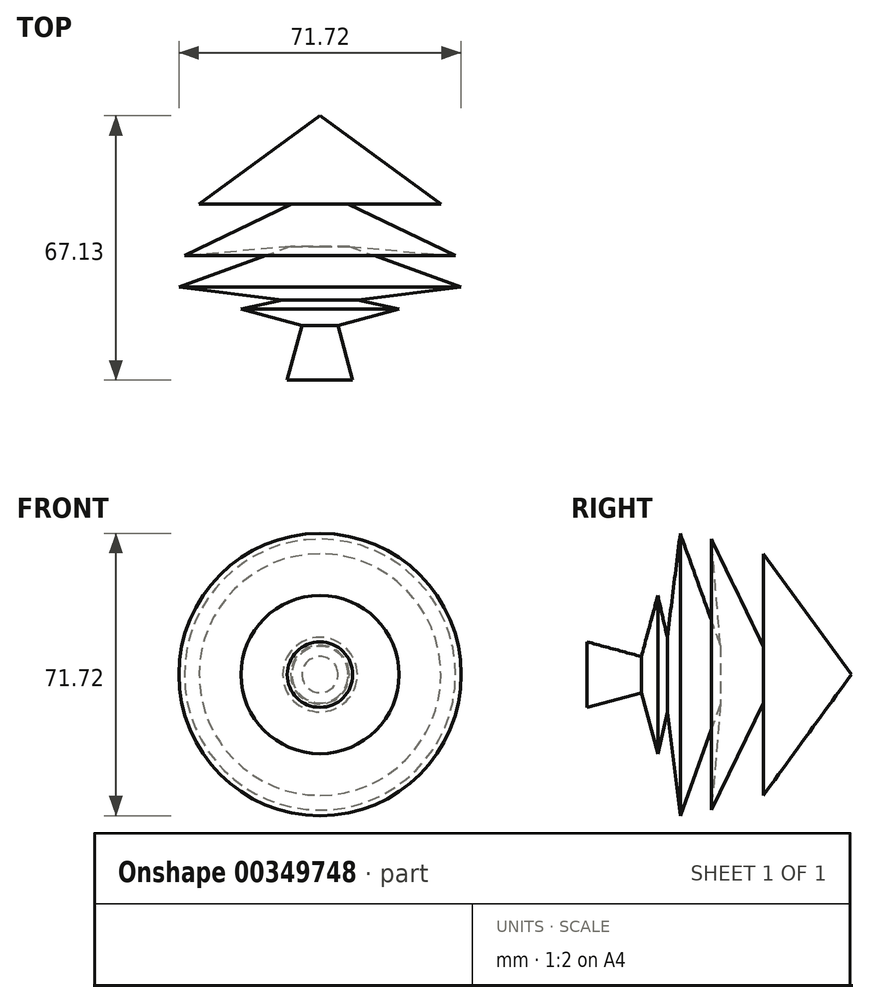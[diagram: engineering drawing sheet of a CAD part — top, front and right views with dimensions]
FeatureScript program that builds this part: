
annotation { "Feature Type Name" : "Feature", "Feature Type Description" : "" }
export const myFeature = defineFeature(function(context is Context, id is Id, definition is map)
    precondition{}
    {
        {
            var Q0;
            Q0=qCreatedBy(makeId("Top.planeOp"),FACE);
            var sketch = newSketch(context, id + "F0", { "sketchPlane" : qUnion([Q0])});
            skLineSegment(sketch, "E0", {"start": v(-8.32, -23.67) * mm, "end": v(-4.6, -9.9) * mm});
            skLineSegment(sketch, "E1", {"start": v(-4.6, -9.9) * mm, "end": v(-20.09, -5.7) * mm});
            skLineSegment(sketch, "E2", {"start": v(-20.09, -5.7) * mm, "end": v(-9.47, -3.3) * mm});
            skLineSegment(sketch, "E3", {"start": v(-9.47, -3.3) * mm, "end": v(-35.86, 0) * mm});
            skLineSegment(sketch, "E4", {"start": v(-35.86, 0) * mm, "end": v(-7.46, 10.18) * mm});
            skLineSegment(sketch, "E5", {"start": v(-7.46, 10.18) * mm, "end": v(-34.43, 7.89) * mm});
            skLineSegment(sketch, "E6", {"start": v(-34.43, 7.89) * mm, "end": v(-7.17, 21.09) * mm});
            skLineSegment(sketch, "E7", {"start": v(-7.17, 21.09) * mm, "end": v(-30.7, 21.09) * mm});
            skLineSegment(sketch, "E8", {"start": v(-30.7, 21.09) * mm, "end": v(0, 43.46) * mm});
            skLineSegment(sketch, "E9", {"start": v(0, 51.5) * mm, "end": v(0, -33.14) * mm});
            skLineSegment(sketch, "E10", {"start": v(-8.32, -23.67) * mm, "end": v(0, -23.67) * mm});
            skSolve(sketch);
        }
        {
            var Q0;
            Q0=makeQuery(id+"F0.imprint","IMPRINT",FACE,{"disambiguationData":[TD([[makeQuery(id+"F0.imprint","IMPRINT",EDGE,{"derivedFrom":sQuery(id+"F0.wireOp",EDGE,"E0")}),-1.0]])]});
            var Q1;
            Q1=sQuery(id+"F0.wireOp",EDGE,"E9");
            revolve(context, id + "F1", {"entities" : qUnion([Q0]), "axis" : qUnion([Q1]), "revolveType" : RevolveType.FULL});
        }
    });
